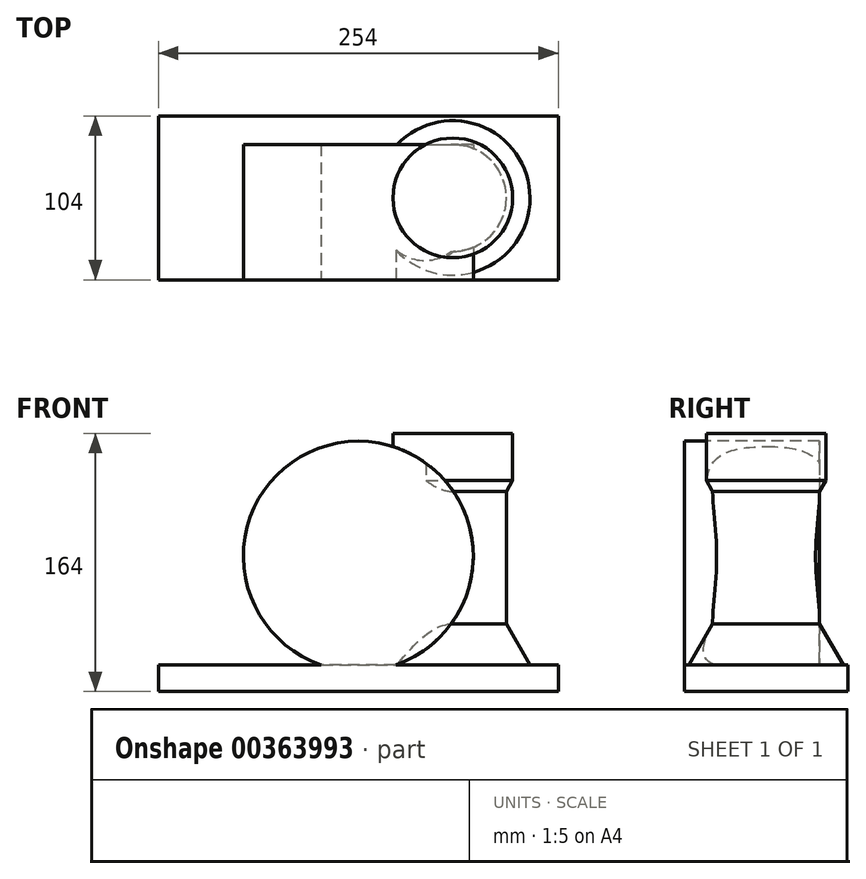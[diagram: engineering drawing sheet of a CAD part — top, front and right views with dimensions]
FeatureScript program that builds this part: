
annotation { "Feature Type Name" : "Feature", "Feature Type Description" : "" }
export const myFeature = defineFeature(function(context is Context, id is Id, definition is map)
    precondition{}
    {
        {
            var Q0;
            Q0=qCreatedBy(makeId("Front.planeOp"),FACE);
            var sketch = newSketch(context, id + "F0", { "sketchPlane" : qUnion([Q0])});
            skCircle(sketch, "E0", {"center": v(0, 86) * mm, "radius": 73 * mm});
            skSolve(sketch);
        }
        {
            var Q0;
            Q0 = qSketchRegion(id + "F0", true);
            extrude(context, id + "F1", {"entities" : qUnion([Q0]), "oppositeDirection" : true, "depth" : 86 * mm});
        }
        {
            var Q0;
            Q0=qCreatedBy(makeId("Front.planeOp"),FACE);
            cPlane(context, id + "F2", {"entities" : qUnion([Q0]), "cplaneType" : CPlaneType.OFFSET, "offset" : (26 * 2) * mm, "oppositeDirection" : true, "width" : 150 * mm, "height" : 150 * mm});
        }
        {
            var Q0;
            Q0=qCreatedBy(id+"F2.planeOp",FACE);
            var sketch = newSketch(context, id + "F3", { "sketchPlane" : qUnion([Q0])});
            skLineSegment(sketch, "E1", {"start": v(60, 164) * mm, "end": v(98, 164) * mm});
            skLineSegment(sketch, "E2", {"start": v(98, 164) * mm, "end": v(98, 133.93) * mm});
            skLineSegment(sketch, "E3", {"start": v(94, 127) * mm, "end": v(98, 133.93) * mm});
            skLineSegment(sketch, "E4", {"start": v(94, 127) * mm, "end": v(94, 43) * mm});
            skLineSegment(sketch, "E5", {"start": v(94, 43) * mm, "end": v(109.01, 17) * mm});
            skLineSegment(sketch, "E6", {"start": v(109.01, 17) * mm, "end": v(60, 17) * mm});
            skLineSegment(sketch, "E7", {"start": v(60, 17) * mm, "end": v(60, 164) * mm});
            skSolve(sketch);
        }
        {
            var Q0;
            Q0 = qSketchRegion(id + "F3", true);
            var Q1;
            Q1=sQuery(id+"F3.wireOp",EDGE,"E7");
            revolve(context, id + "F4", {"operationType" : NewBodyOperationType.ADD, "entities" : qUnion([Q0]), "axis" : qUnion([Q1]), "revolveType" : RevolveType.FULL});
        }
        {
            var Q0;
            Q0=qCreatedBy(makeId("Top.planeOp"),FACE);
            var sketch = newSketch(context, id + "F5", { "sketchPlane" : qUnion([Q0])});
            skLineSegment(sketch, "E8.bottom", {"start": v(-127, 104) * mm, "end": v(127, 104) * mm});
            skLineSegment(sketch, "E8.top", {"start": v(-127, 0) * mm, "end": v(127, 0) * mm});
            skLineSegment(sketch, "E8.left", {"start": v(-127, 104) * mm, "end": v(-127, 0) * mm});
            skLineSegment(sketch, "E8.right", {"start": v(127, 104) * mm, "end": v(127, 0) * mm});
            skSolve(sketch);
        }
        {
            var Q0;
            Q0 = qSketchRegion(id + "F5", true);
            extrude(context, id + "F6", {"entities" : qUnion([Q0]), "operationType" : NewBodyOperationType.ADD, "depth" : (8.5 * 2) * mm});
        }
    });
